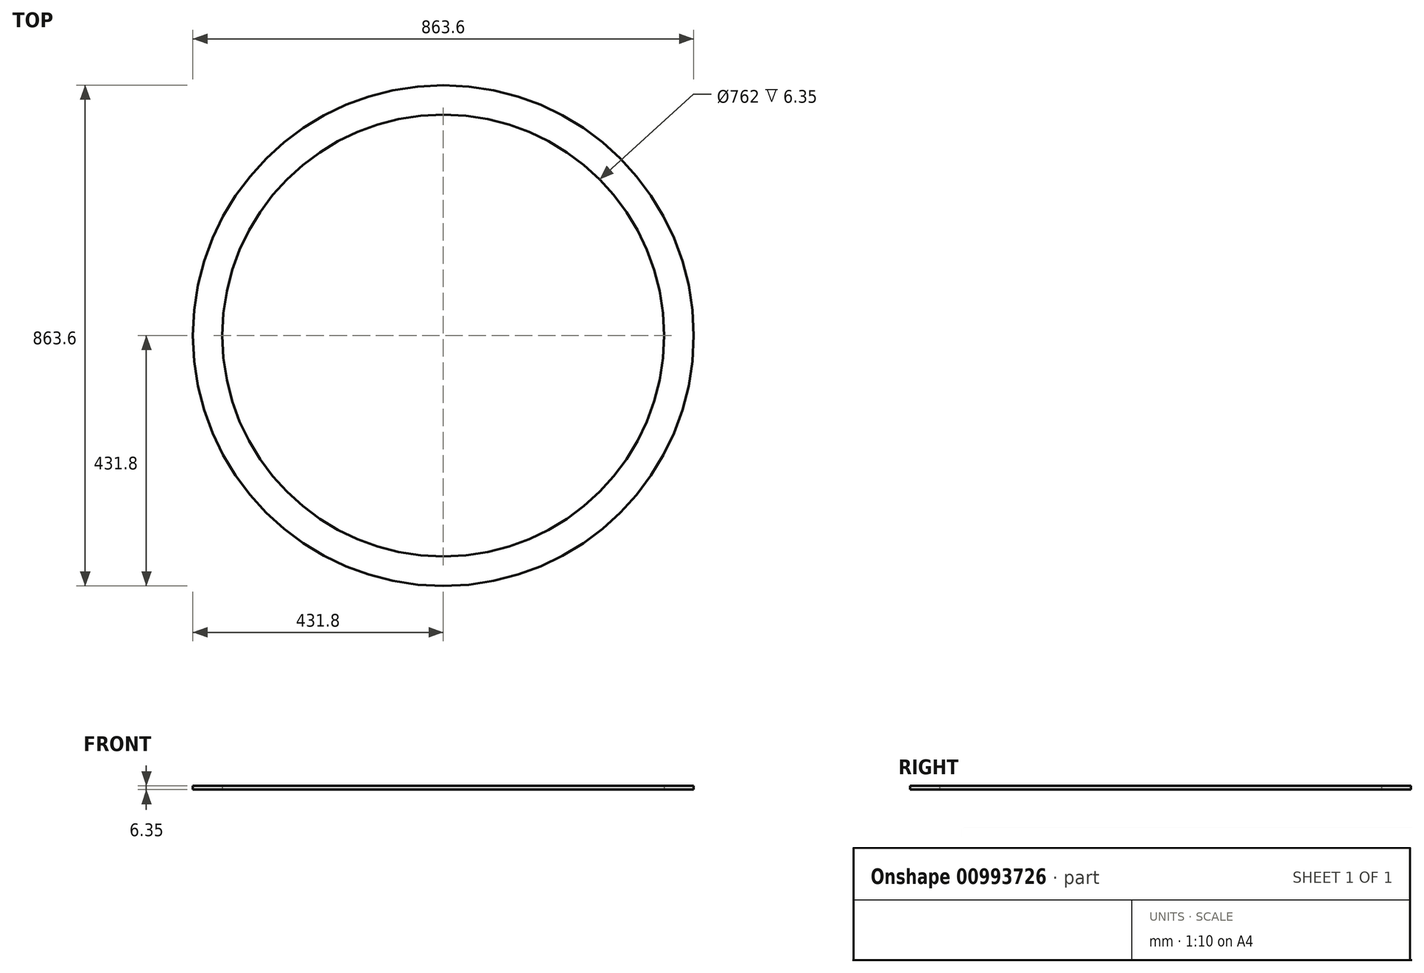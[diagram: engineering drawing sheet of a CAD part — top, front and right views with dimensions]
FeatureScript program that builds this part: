
annotation { "Feature Type Name" : "Feature", "Feature Type Description" : "" }
export const myFeature = defineFeature(function(context is Context, id is Id, definition is map)
    precondition{}
    {
        {
            var Q0;
            Q0=qCreatedBy(makeId("Top.planeOp"),FACE);
            var sketch = newSketch(context, id + "F0", { "sketchPlane" : qUnion([Q0])});
            skCircle(sketch, "E0", {"center": v(0, 0) * mm, "radius": 431.8 * mm});
            skCircle(sketch, "E1", {"center": v(0, 0) * mm, "radius": 381 * mm});
            skSolve(sketch);
        }
        {
            var Q0;
            Q0=makeQuery(id+"F0.imprint","IMPRINT",FACE,{"disambiguationData":[TD([[makeQuery(id+"F0.imprint","IMPRINT",EDGE,{"derivedFrom":sQuery(id+"F0.wireOp",EDGE,"E0")}),1.0]])]});
            extrude(context, id + "F1", {"entities" : qUnion([Q0]), "depth" : 6.35 * mm, "offsetDistance" : 25.4 * mm});
        }
    });
